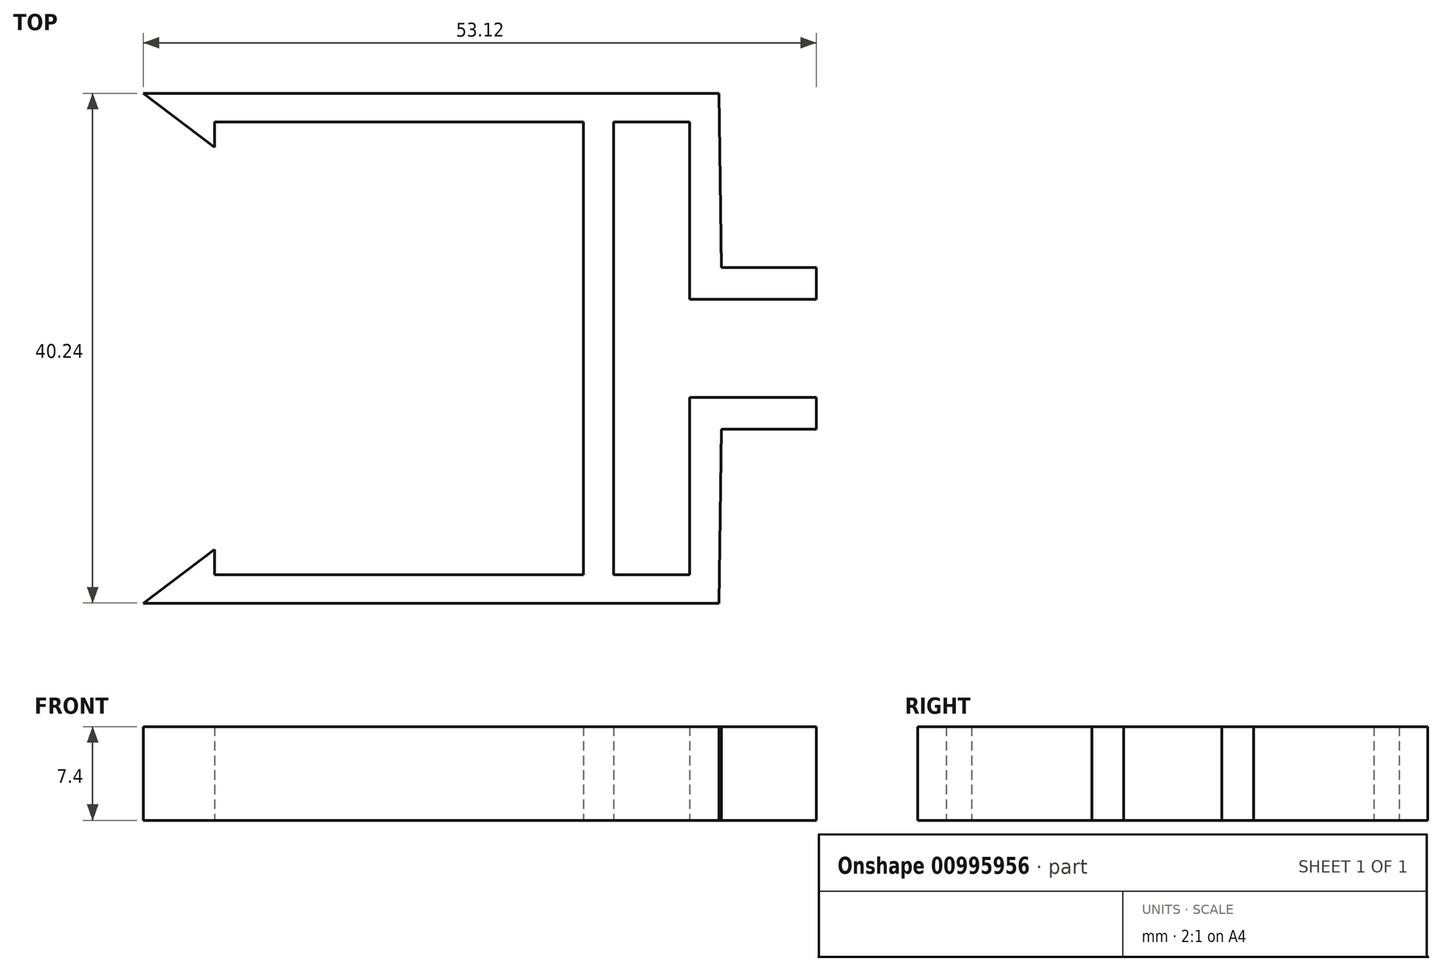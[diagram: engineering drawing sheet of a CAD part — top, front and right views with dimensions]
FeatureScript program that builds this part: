
annotation { "Feature Type Name" : "Feature", "Feature Type Description" : "" }
export const myFeature = defineFeature(function(context is Context, id is Id, definition is map)
    precondition{}
    {
        {
            var Q0;
            Q0=qCreatedBy(makeId("Top.planeOp"),FACE);
            var sketch = newSketch(context, id + "F0", { "sketchPlane" : qUnion([Q0])});
            skLineSegment(sketch, "E0.bottom", {"start": v(-1.2, 17.88) * mm, "end": v(1.2, 17.88) * mm});
            skLineSegment(sketch, "E0.top", {"start": v(-1.2, -17.88) * mm, "end": v(1.2, -17.88) * mm});
            skLineSegment(sketch, "E0.left", {"start": v(-1.2, 17.88) * mm, "end": v(-1.2, -17.88) * mm});
            skLineSegment(sketch, "E0.right", {"start": v(1.2, 17.88) * mm, "end": v(1.2, -17.88) * mm});
            skLineSegment(sketch, "E1", {"start": v(-1.2, 17.88) * mm, "end": v(-30.3, 17.87) * mm});
            skLineSegment(sketch, "E2", {"start": v(-1.2, -17.88) * mm, "end": v(-30.3, -17.88) * mm});
            skLineSegment(sketch, "E3", {"start": v(-30.3, -17.88) * mm, "end": v(-30.3, -20.13) * mm});
            skLineSegment(sketch, "E4", {"start": v(-30.3, -20.13) * mm, "end": v(49.7, -20.13) * mm});
            skLineSegment(sketch, "E5", {"start": v(-30.3, 17.87) * mm, "end": v(-30.3, 20.12) * mm});
            skLineSegment(sketch, "E6", {"start": v(-30.3, 20.12) * mm, "end": v(49.7, 20.12) * mm});
            skLineSegment(sketch, "E7", {"start": v(-30.3, -17.88) * mm, "end": v(-30.3, -15.88) * mm});
            skLineSegment(sketch, "E8", {"start": v(-30.3, -15.88) * mm, "end": v(-35.92, -20.13) * mm});
            skLineSegment(sketch, "E9", {"start": v(-35.92, -20.13) * mm, "end": v(-30.3, -20.13) * mm});
            skLineSegment(sketch, "E10.MirrorCS", {"start": v(-35.92, 20.13) * mm, "end": v(-30.3, 20.13) * mm});
            skLineSegment(sketch, "E11.MirrorCS", {"start": v(-30.3, 15.88) * mm, "end": v(-35.92, 20.13) * mm});
            skLineSegment(sketch, "E12.MirrorCS", {"start": v(-30.3, 17.88) * mm, "end": v(-30.3, 20.13) * mm});
            skLineSegment(sketch, "E13.MirrorCS", {"start": v(-30.3, 17.88) * mm, "end": v(-30.3, 15.88) * mm});
            skLineSegment(sketch, "E14", {"start": v(1.2, 17.88) * mm, "end": v(7.2, 17.88) * mm});
            skLineSegment(sketch, "E15", {"start": v(7.2, 17.88) * mm, "end": v(7.2, 3.88) * mm});
            skLineSegment(sketch, "E16", {"start": v(7.2, 3.88) * mm, "end": v(17.2, 3.88) * mm});
            skLineSegment(sketch, "E17", {"start": v(17.2, 3.88) * mm, "end": v(17.2, 6.38) * mm});
            skLineSegment(sketch, "E18", {"start": v(17.2, 6.38) * mm, "end": v(9.7, 6.38) * mm});
            skLineSegment(sketch, "E19", {"start": v(9.7, 6.38) * mm, "end": v(9.53, 20.12) * mm});
            skLineSegment(sketch, "E20.MirrorCS", {"start": v(17.2, -3.88) * mm, "end": v(17.2, -6.38) * mm});
            skLineSegment(sketch, "E21.MirrorCS", {"start": v(7.2, -3.88) * mm, "end": v(17.2, -3.88) * mm});
            skLineSegment(sketch, "E22.MirrorCS", {"start": v(7.2, -17.88) * mm, "end": v(7.2, -3.88) * mm});
            skLineSegment(sketch, "E23.MirrorCS", {"start": v(9.7, -6.38) * mm, "end": v(9.53, -20.12) * mm});
            skLineSegment(sketch, "E24.MirrorCS", {"start": v(17.2, -6.38) * mm, "end": v(9.7, -6.38) * mm});
            skLineSegment(sketch, "E25.MirrorCS", {"start": v(1.2, -17.88) * mm, "end": v(7.2, -17.88) * mm});
            skLineSegment(sketch, "E26", {"start": v(4.2, 17.88) * mm, "end": v(7.2, 15.33) * mm});
            skLineSegment(sketch, "E27.MirrorCS", {"start": v(4.2, -17.88) * mm, "end": v(7.2, -15.33) * mm});
            skSolve(sketch);
        }
        {
            var Q0;
            {var subQ6=sQuery(id+"F0.wireOp",EDGE,"E0.top");Q0=makeQuery(id+"F0.imprint","IMPRINT",FACE,{"disambiguationData":[TD([[makeQuery(id+"F0.imprint","IMPRINT",EDGE,{"derivedFrom":subQ6}),-1.0]])]});}
            var Q1;
            Q1=makeQuery(id+"F0.imprint","IMPRINT",FACE,{"disambiguationData":[TD([[makeQuery(id+"F0.imprint","IMPRINT",EDGE,{"derivedFrom":sQuery(id+"F0.wireOp",EDGE,"E0.bottom")}),-1.0]])]});
            var Q2;
            {var subQ7=sQuery(id+"F0.wireOp",EDGE,"E0.bottom");Q2=makeQuery(id+"F0.imprint","IMPRINT",FACE,{"disambiguationData":[TD([[makeQuery(id+"F0.imprint","IMPRINT",EDGE,{"derivedFrom":subQ7}),1.0]])]});}
            var Q3;
            Q3=makeQuery(id+"F0.imprint","IMPRINT",FACE,{"disambiguationData":[TD([[makeQuery(id+"F0.imprint","IMPRINT",EDGE,{"derivedFrom":sQuery(id+"F0.wireOp",EDGE,"E10.MirrorCS")}),-1.0]])]});
            var Q4;
            Q4=makeQuery(id+"F0.imprint","IMPRINT",FACE,{"disambiguationData":[TD([[makeQuery(id+"F0.imprint","IMPRINT",EDGE,{"derivedFrom":sQuery(id+"F0.wireOp",EDGE,"E3")}),-1.0]])]});
            extrude(context, id + "F1", {"entities" : qUnion([Q0, Q1, Q2, Q3, Q4]), "depth" : 7.4 * mm, "offsetDistance" : 25 * mm});
        }
    });
